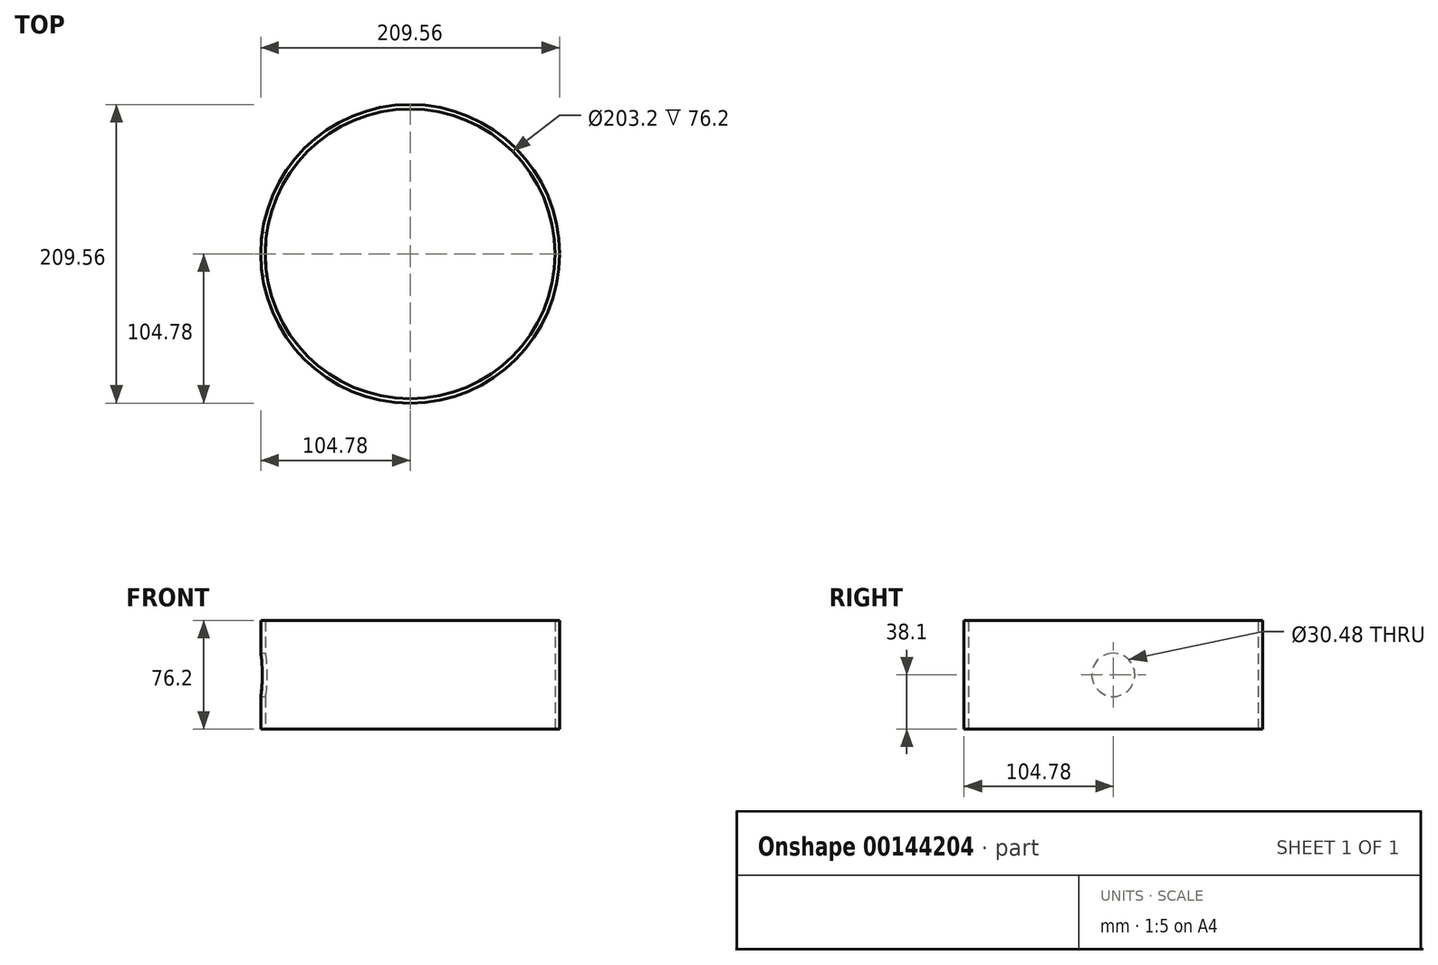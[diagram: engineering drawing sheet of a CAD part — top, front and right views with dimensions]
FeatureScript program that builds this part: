
annotation { "Feature Type Name" : "Feature", "Feature Type Description" : "" }
export const myFeature = defineFeature(function(context is Context, id is Id, definition is map)
    precondition{}
    {
        {
            var Q0;
            Q0=qCreatedBy(makeId("Top.planeOp"),FACE);
            var sketch = newSketch(context, id + "F0", { "sketchPlane" : qUnion([Q0])});
            skCircle(sketch, "E0", {"center": v(0, 0) * mm, "radius": 104.78 * mm});
            skCircle(sketch, "E1", {"center": v(0, 0) * mm, "radius": 101.6 * mm});
            skSolve(sketch);
        }
        {
            var Q0;
            Q0=qSketchRegion(id+"F0",true);
            extrude(context, id + "F1", {"entities" : qUnion([Q0]), "endBound" : BoundingType.SYMMETRIC, "depth" : 76.2 * mm});
        }
        {
            var Q0;
            Q0=qCreatedBy(makeId("Right.planeOp"),FACE);
            var sketch = newSketch(context, id + "F2", { "sketchPlane" : qUnion([Q0])});
            skCircle(sketch, "E2", {"center": v(0, 0) * mm, "radius": 15.24 * mm});
            skSolve(sketch);
        }
        {
            var Q0;
            Q0=qSketchRegion(id+"F2",true);
            extrude(context, id + "F3", {"entities" : qUnion([Q0]), "operationType" : NewBodyOperationType.REMOVE, "endBound" : BoundingType.THROUGH_ALL, "oppositeDirection" : true, "depth" : 25.4 * mm});
        }
    });
